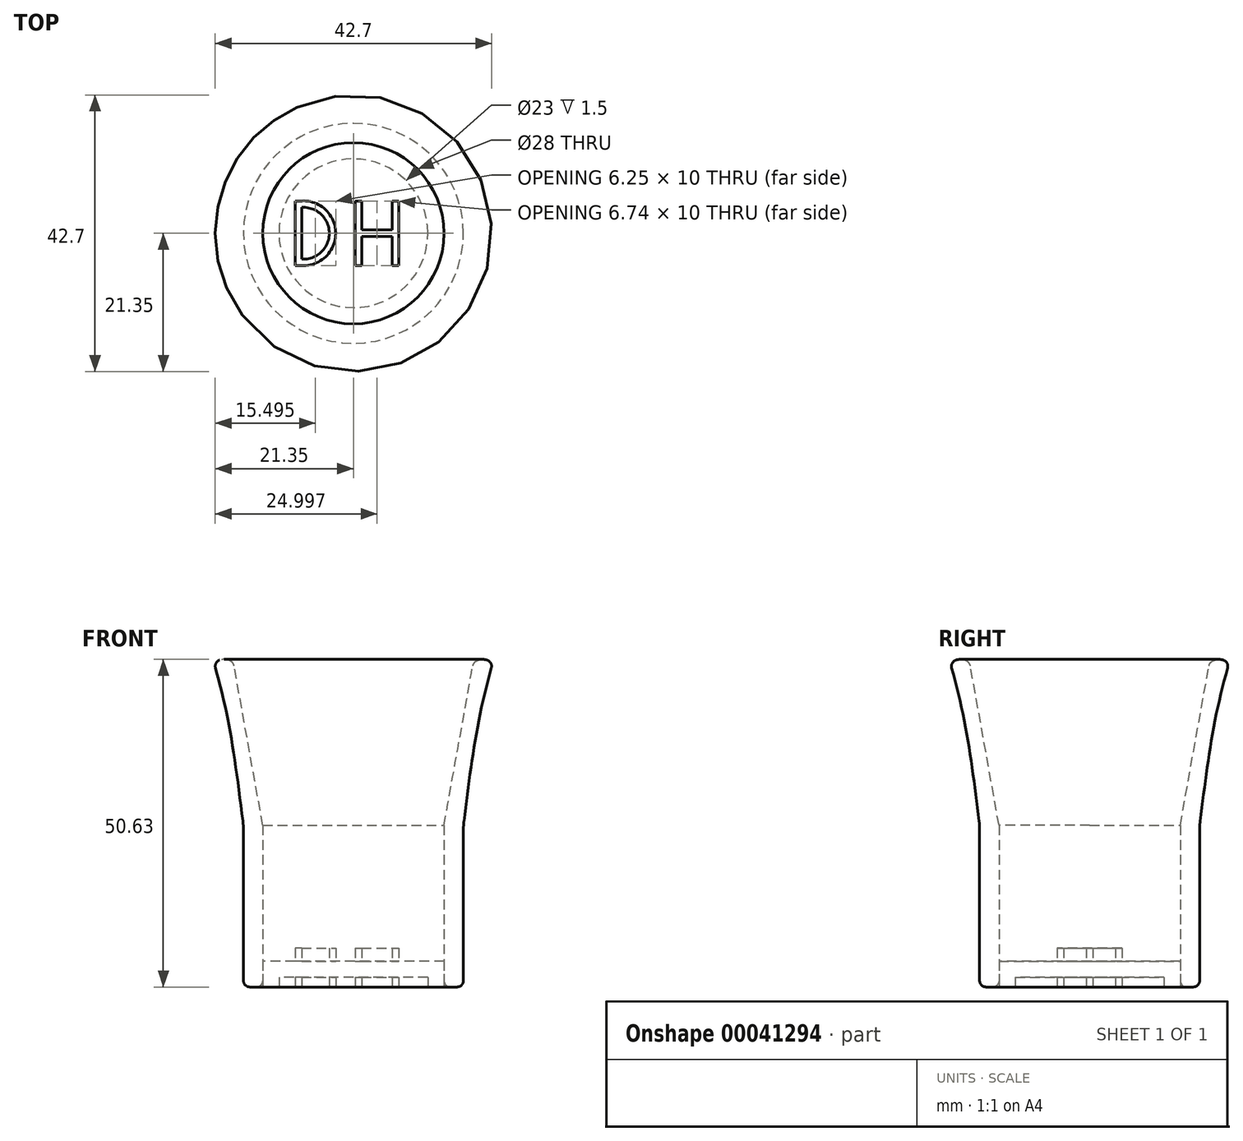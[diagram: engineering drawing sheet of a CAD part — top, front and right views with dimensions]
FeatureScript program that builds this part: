
annotation { "Feature Type Name" : "Feature", "Feature Type Description" : "" }
export const myFeature = defineFeature(function(context is Context, id is Id, definition is map)
    precondition{}
    {
        {
            var Q0;
            Q0=qCreatedBy(makeId("Top.planeOp"),FACE);
            var sketch = newSketch(context, id + "F0", { "sketchPlane" : qUnion([Q0])});
            skCircle(sketch, "E0", {"center": v(0, 0) * mm, "radius": 14 * mm});
            skCircle(sketch, "E1", {"center": v(0, 0) * mm, "radius": 21.5 * mm});
            skLineSegment(sketch, "E2", {"start": v(-8.98, 5) * mm, "end": v(-8.98, -5) * mm});
            skLineSegment(sketch, "E3", {"start": v(-8.98, -5) * mm, "end": v(-8, -5) * mm});
            skLineSegment(sketch, "E4", {"start": v(-8, -4) * mm, "end": v(-8, 4) * mm});
            skLineSegment(sketch, "E5", {"start": v(-8, 5) * mm, "end": v(-8.98, 5) * mm});
            skLineSegment(sketch, "E6", {"start": v(-21.5, 0) * mm, "end": v(21.5, 0) * mm, "construction": true});
            skLineSegment(sketch, "E7", {"start": v(-11.18, -5) * mm, "end": v(11.18, -5) * mm, "construction": true});
            skLineSegment(sketch, "E8", {"start": v(-11.18, 5) * mm, "end": v(11.18, 5) * mm, "construction": true});
            skLineSegment(sketch, "E9", {"start": v(0, 5) * mm, "end": v(0, -5) * mm, "construction": true});
            skLineSegment(sketch, "E10", {"start": v(-11.18, 4) * mm, "end": v(11.18, 4) * mm, "construction": true});
            skLineSegment(sketch, "E11", {"start": v(-11.18, -4) * mm, "end": v(11.18, -4) * mm, "construction": true});
            skArc(sketch, "E12", {"start": v(-8, -5) * mm, "mid": v(-2.73, 0) * mm, "end": v(-8, 5) * mm});
            skArc(sketch, "E13", {"start": v(-8, -4) * mm, "mid": v(-3.73, 0) * mm, "end": v(-8, 4) * mm});
            skLineSegment(sketch, "E14", {"start": v(0.28, 5) * mm, "end": v(0.28, -5) * mm});
            skLineSegment(sketch, "E15", {"start": v(0.28, -5) * mm, "end": v(1.28, -5) * mm});
            skLineSegment(sketch, "E16", {"start": v(1.28, -5) * mm, "end": v(1.28, -0.5) * mm});
            skLineSegment(sketch, "E17", {"start": v(3.85, 5) * mm, "end": v(1.28, 5) * mm});
            skLineSegment(sketch, "E18", {"start": v(6.02, 5) * mm, "end": v(6.02, 0.5) * mm});
            skLineSegment(sketch, "E19", {"start": v(6.02, -5) * mm, "end": v(7.02, -5) * mm});
            skLineSegment(sketch, "E20", {"start": v(7.02, -5) * mm, "end": v(7.02, 5) * mm});
            skLineSegment(sketch, "E21", {"start": v(9.62, 5) * mm, "end": v(7.02, 5) * mm});
            skLineSegment(sketch, "E22", {"start": v(1.28, 0.5) * mm, "end": v(6.02, 0.5) * mm});
            skLineSegment(sketch, "E23", {"start": v(6.02, -0.5) * mm, "end": v(1.28, -0.5) * mm});
            skLineSegment(sketch, "E24.trimOffspring", {"start": v(1.28, 0.5) * mm, "end": v(1.28, 5) * mm});
            skLineSegment(sketch, "E25.trimOffspring", {"start": v(6.02, -0.5) * mm, "end": v(6.02, -5) * mm});
            skPoint(sketch, "E26", {"position": v(14, 0) * mm});
            skPoint(sketch, "E27", {"position": v(-14, 0) * mm});
            skLineSegment(sketch, "E28", {"start": v(0.28, 5) * mm, "end": v(1.28, 5) * mm});
            skLineSegment(sketch, "E29", {"start": v(6.02, 5) * mm, "end": v(7.02, 5) * mm});
            skSolve(sketch);
        }
        {
            var Q0;
            Q0=makeQuery(id+"F0.imprint","IMPRINT",FACE,{"disambiguationData":[TD([[makeQuery(id+"F0.imprint","IMPRINT",EDGE,{"derivedFrom":sQuery(id+"F0.wireOp",EDGE,"E2")}),1.0]])]});
            var Q1;
            {var subQ2=sQuery(id+"F0.wireOp",EDGE,"E14");Q1=makeQuery(id+"F0.imprint","IMPRINT",FACE,{"disambiguationData":[TD([[makeQuery(id+"F0.imprint","IMPRINT",EDGE,{"derivedFrom":subQ2}),1.0]])]});}
            extrude(context, id + "F1", {"entities" : qUnion([Q0, Q1]), "depth" : 6 * mm});
        }
        {
            var Q0;
            Q0=makeQuery(id+"F0.imprint","IMPRINT",FACE,{"disambiguationData":[TD([[makeQuery(id+"F0.imprint","IMPRINT",EDGE,{"derivedFrom":sQuery(id+"F0.wireOp",EDGE,"E0")}),1.0]])]});
            var Q1;
            Q1=makeQuery(id+"F0.imprint","IMPRINT",FACE,{"disambiguationData":[TD([[makeQuery(id+"F0.imprint","IMPRINT",EDGE,{"derivedFrom":sQuery(id+"F0.wireOp",EDGE,"E4")}),-1.0]])]});
            extrude(context, id + "F2", {"entities" : qUnion([Q0, Q1]), "operationType" : NewBodyOperationType.ADD, "depth" : 4 * mm});
        }
        {
            var Q0;
            {var subQ0=sQuery(id+"F0.wireOp",EDGE,"E2");var subQ1=sQuery(id+"F0.wireOp",EDGE,"E3");var subQ2=sQuery(id+"F0.wireOp",EDGE,"E4");var subQ3=sQuery(id+"F0.wireOp",EDGE,"E5");var subQ4=sQuery(id+"F0.wireOp",EDGE,"E12");var subQ5=sQuery(id+"F0.wireOp",EDGE,"E13");var subQ6=sQuery(id+"F0.wireOp",EDGE,"E14");var subQ7=sQuery(id+"F0.wireOp",EDGE,"E15");var subQ8=sQuery(id+"F0.wireOp",EDGE,"E16");var subQ9=sQuery(id+"F0.wireOp",EDGE,"E17");var subQ10=sQuery(id+"F0.wireOp",EDGE,"E18");var subQ11=sQuery(id+"F0.wireOp",EDGE,"E19");var subQ12=sQuery(id+"F0.wireOp",EDGE,"E20");var subQ13=sQuery(id+"F0.wireOp",EDGE,"E21");var subQ14=sQuery(id+"F0.wireOp",EDGE,"E22");var subQ15=sQuery(id+"F0.wireOp",EDGE,"E23");var subQ16=sQuery(id+"F0.wireOp",EDGE,"E24.trimOffspring");var subQ17=sQuery(id+"F0.wireOp",EDGE,"E25.trimOffspring");Q0=makeQuery(id+"F2.boolean.opBoolean","MERGE",FACE,{"derivedFrom":[makeQuery(id+"F1.opExtrude","CAP_FACE",FACE,{"disambiguationData":[OSD([subQ0,subQ1,subQ2,subQ3,subQ4,subQ5])],"isStart":true}),makeQuery(id+"F1.opExtrude","CAP_FACE",FACE,{"disambiguationData":[OSD([subQ6,subQ7,subQ8,subQ9,subQ10,subQ11,subQ12,subQ13,subQ14,subQ15,subQ16,subQ17])],"isStart":true}),makeQuery(id+"F2.opExtrude","CAP_FACE",FACE,{"disambiguationData":[OSD([sQuery(id+"F0.wireOp",EDGE,"E0"),subQ0,subQ1,subQ3,subQ4,subQ6,subQ7,subQ8,subQ9,subQ10,subQ11,subQ12,subQ13,subQ14,subQ15,subQ16,subQ17])],"isStart":true}),makeQuery(id+"F2.opExtrude","CAP_FACE",FACE,{"disambiguationData":[OSD([subQ2,subQ5])],"isStart":true})]});}
            var Q1;
            Q1=makeQuery(id+"F1.opExtrude","SWEPT_BODY",BODY,{"disambiguationData":[OSD([sQuery(id+"F0.wireOp",EDGE,"E2"),sQuery(id+"F0.wireOp",EDGE,"E3"),sQuery(id+"F0.wireOp",EDGE,"E4"),sQuery(id+"F0.wireOp",EDGE,"E5"),sQuery(id+"F0.wireOp",EDGE,"E12"),sQuery(id+"F0.wireOp",EDGE,"E13")])]});
            shell(context, id + "F3", {"entities" : qUnion([Q0]), "parts" : qUnion([Q1]), "thickness" : 2.5 * mm});
        }
        {
            var Q0;
            Q0=makeQuery(id+"F0.imprint","IMPRINT",FACE,{"disambiguationData":[TD([[makeQuery(id+"F0.imprint","IMPRINT",EDGE,{"derivedFrom":sQuery(id+"F0.wireOp",EDGE,"E2")}),1.0]])]});
            var Q1;
            {var subQ2=sQuery(id+"F0.wireOp",EDGE,"E14");Q1=makeQuery(id+"F0.imprint","IMPRINT",FACE,{"disambiguationData":[TD([[makeQuery(id+"F0.imprint","IMPRINT",EDGE,{"derivedFrom":subQ2}),1.0]])]});}
            var Q2;
            Q2=makeQuery(id+"F3.opShell","OFFSET_FACE",FACE,{"disambiguationData":[OSD([sQuery(id+"F0.wireOp",EDGE,"E0"),sQuery(id+"F0.wireOp",EDGE,"E2"),sQuery(id+"F0.wireOp",EDGE,"E3"),sQuery(id+"F0.wireOp",EDGE,"E4"),sQuery(id+"F0.wireOp",EDGE,"E5"),sQuery(id+"F0.wireOp",EDGE,"E12"),sQuery(id+"F0.wireOp",EDGE,"E13"),sQuery(id+"F0.wireOp",EDGE,"E14"),sQuery(id+"F0.wireOp",EDGE,"E15"),sQuery(id+"F0.wireOp",EDGE,"E16"),sQuery(id+"F0.wireOp",EDGE,"E17"),sQuery(id+"F0.wireOp",EDGE,"E18"),sQuery(id+"F0.wireOp",EDGE,"E19"),sQuery(id+"F0.wireOp",EDGE,"E20"),sQuery(id+"F0.wireOp",EDGE,"E21"),sQuery(id+"F0.wireOp",EDGE,"E22"),sQuery(id+"F0.wireOp",EDGE,"E23"),sQuery(id+"F0.wireOp",EDGE,"E24.trimOffspring"),sQuery(id+"F0.wireOp",EDGE,"E25.trimOffspring")])]});
            extrude(context, id + "F4", {"entities" : qUnion([Q0, Q1]), "operationType" : NewBodyOperationType.ADD, "endBound" : BoundingType.UP_TO_SURFACE, "endBoundEntityFace" : qUnion([Q2]), "depth" : .5 * mm});
        }
        {
            var Q0;
            Q0=qCreatedBy(makeId("Front.planeOp"),FACE);
            var sketch = newSketch(context, id + "F5", { "sketchPlane" : qUnion([Q0])});
            skPoint(sketch, "E30", {"position": v(-21.5, 0) * mm});
            skLineSegment(sketch, "E31", {"start": v(-21.5, 50) * mm, "end": v(-21.5, 0) * mm, "construction": true});
            skLineSegment(sketch, "E32", {"start": v(21.5, 50) * mm, "end": v(21.5, 0) * mm, "construction": true});
            skLineSegment(sketch, "E33", {"start": v(14, 0) * mm, "end": v(14, 50) * mm, "construction": true});
            skLineSegment(sketch, "E34", {"start": v(-14, 0) * mm, "end": v(-14, 50) * mm, "construction": true});
            skLineSegment(sketch, "E35", {"start": v(18.5, 0) * mm, "end": v(18.5, 50) * mm, "construction": true});
            skLineSegment(sketch, "E36", {"start": v(-18.5, 0) * mm, "end": v(-18.5, 50) * mm, "construction": true});
            skPoint(sketch, "E37", {"position": v(14, 4) * mm});
            skPoint(sketch, "E38", {"position": v(-14, 4) * mm});
            skLineSegment(sketch, "E39", {"start": v(17, 0) * mm, "end": v(17, 50) * mm, "construction": true});
            skLineSegment(sketch, "E40", {"start": v(-17, 0) * mm, "end": v(-17, 50) * mm, "construction": true});
            skLineSegment(sketch, "E41", {"start": v(0, 0) * mm, "end": v(0, 52.53) * mm, "construction": true});
            skLineSegment(sketch, "E42", {"start": v(14, 0) * mm, "end": v(17, 0) * mm});
            skArc(sketch, "E43", {"start": v(21.5, 50) * mm, "mid": v(20, 50.63) * mm, "end": v(18.5, 50) * mm});
            skLineSegment(sketch, "E44", {"start": v(14, 4) * mm, "end": v(14, 0) * mm});
            skPoint(sketch, "E45", {"position": v(14, 25) * mm});
            skLineSegment(sketch, "E46", {"start": v(14, 4) * mm, "end": v(14, 25) * mm});
            skLineSegment(sketch, "E47", {"start": v(17, 0) * mm, "end": v(17, 25) * mm});
            skFitSpline(sketch, "E48", {"points": [v(14, 25) * mm, v(18.5, 50) * mm], "startDerivative": vector(4.5, 25) * mm, "endDerivative": vector(4.5, 25) * mm});
            skFitSpline(sketch, "E49", {"points": [v(17, 25) * mm, v(19.25, 40.56) * mm, v(21.5, 50) * mm], "startDerivative": vector(3.71, 29.55) * mm, "endDerivative": vector(5.35, 20.07) * mm});
            skSolve(sketch);
        }
        {
            var Q0;
            Q0=makeQuery(id+"F5.imprint","IMPRINT",FACE,{"disambiguationData":[TD([[makeQuery(id+"F5.imprint","IMPRINT",EDGE,{"derivedFrom":sQuery(id+"F5.wireOp",EDGE,"E42")}),1.0]])]});
            var Q1;
            Q1=sQuery(id+"F5.wireOp",EDGE,"573e663a-d2f6-43b7-b2ef-6b07f1285649");
            var Q2;
            Q2=sQuery(id+"F5.wireOp",EDGE,"37745fba-8d2d-45e3-929c-63e503ee2c1b");
            var Q3;
            Q3=sQuery(id+"F5.wireOp",EDGE,"E43");
            var Q4;
            Q4=sQuery(id+"F5.wireOp",EDGE,"E44");
            var Q5;
            Q5=sQuery(id+"F5.wireOp",EDGE,"E42");
            var Q6;
            Q6=sQuery(id+"F5.wireOp",EDGE,"E41");
            revolve(context, id + "F6", {"entities" : qUnion([Q0]), "surfaceEntities" : qUnion([Q1, Q2, Q3, Q4, Q5]), "axis" : qUnion([Q6]), "revolveType" : RevolveType.FULL});
        }
        {
            var Q0;
            Q0=makeQuery(id+"F6.opRevolve","SWEPT_FACE",FACE,{"disambiguationData":[OSD([sQuery(id+"F5.wireOp",EDGE,"E43")])]});
            var Q1;
            Q1=makeQuery(id+"F6.opRevolve","SWEPT_FACE",FACE,{"disambiguationData":[OSD([sQuery(id+"F5.wireOp",EDGE,"E42")])]});
            fillet(context, id + "F7", {"entities" : qUnion([Q0, Q1]), "radius" : 1 * mm, "tangentPropagation" : true, "allowEdgeOverflow" : false});
        }
        {
            var Q0;
            Q0=makeQuery(id+"F6.opRevolve","SWEPT_FACE",FACE,{"disambiguationData":[OSD([sQuery(id+"F5.wireOp",EDGE,"E49")])]});
            fillet(context, id + "F8", {"entities" : qUnion([Q0]), "radius" : 10 * mm, "tangentPropagation" : true, "allowEdgeOverflow" : false});
        }
    });
